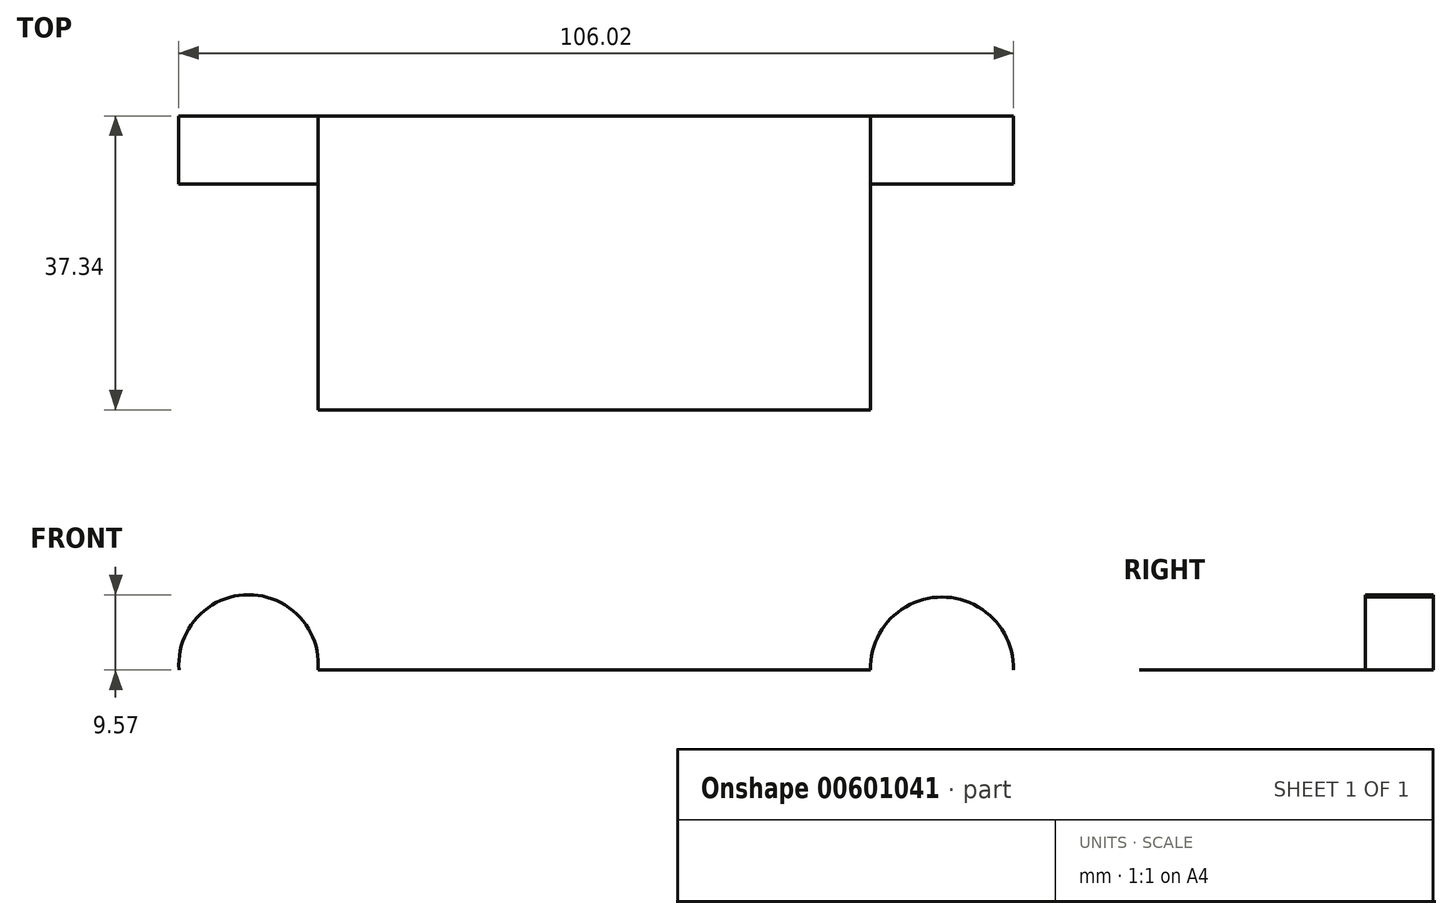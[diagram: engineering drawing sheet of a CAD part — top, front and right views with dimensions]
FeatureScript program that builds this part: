
annotation { "Feature Type Name" : "Feature", "Feature Type Description" : "" }
export const myFeature = defineFeature(function(context is Context, id is Id, definition is map)
    precondition{}
    {
        {
            var Q0;
            Q0=qCreatedBy(makeId("Front.planeOp"),FACE);
            var sketch = newSketch(context, id + "F0", { "sketchPlane" : qUnion([Q0])});
            skLineSegment(sketch, "E0", {"start": v(-53.64, -5.38) * mm, "end": v(16.51, -5.38) * mm});
            skArc(sketch, "E1", {"start": v(34.7, -5.38) * mm, "mid": v(25.6, 3.9) * mm, "end": v(16.51, -5.38) * mm});
            skArc(sketch, "E2", {"start": v(-53.64, -5.38) * mm, "mid": v(-62.47, 4.19) * mm, "end": v(-71.3, -5.38) * mm});
            skSolve(sketch);
        }
        {
            var Q0;
            Q0=sQuery(id+"F0.wireOp",EDGE,"E0");
            extrude(context, id + "F1", {"bodyType" : ToolBodyType.SURFACE, "surfaceEntities" : qUnion([Q0]), "depth" : 37.34 * mm, "offsetDistance" : 25.4 * mm});
        }
        {
            var Q0;
            Q0=sQuery(id+"F0.wireOp",EDGE,"E2");
            extrude(context, id + "F2", {"bodyType" : ToolBodyType.SURFACE, "surfaceEntities" : qUnion([Q0]), "depth" : 8.64 * mm, "offsetDistance" : 25.4 * mm});
        }
        {
            var Q0;
            Q0=sQuery(id+"F0.wireOp",EDGE,"E1");
            extrude(context, id + "F3", {"bodyType" : ToolBodyType.SURFACE, "surfaceEntities" : qUnion([Q0]), "depth" : 8.64 * mm, "offsetDistance" : 25.4 * mm});
        }
    });
